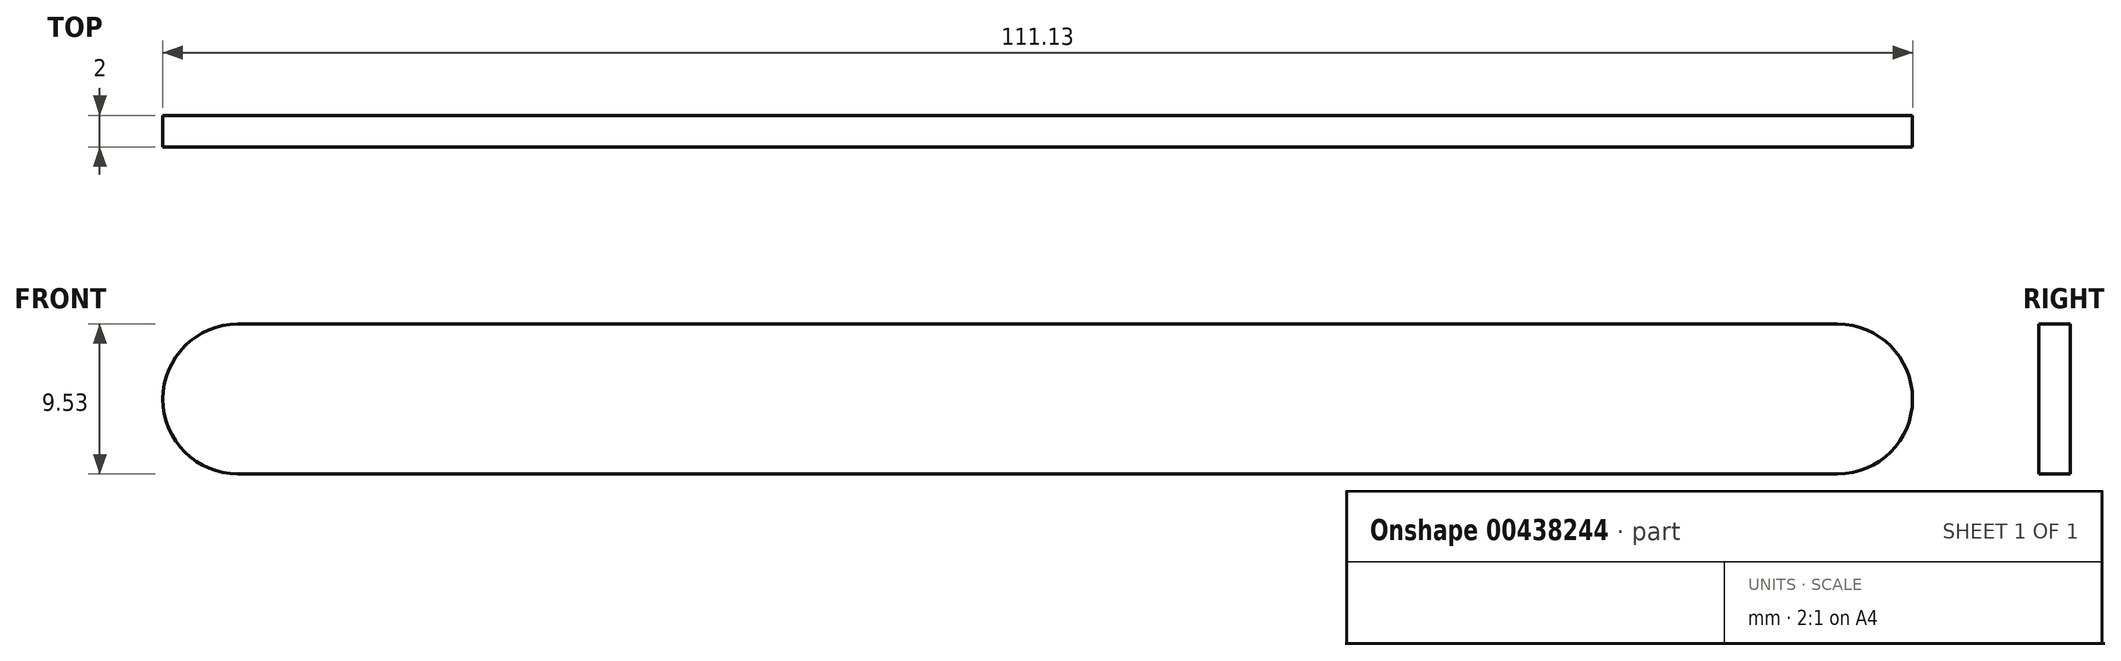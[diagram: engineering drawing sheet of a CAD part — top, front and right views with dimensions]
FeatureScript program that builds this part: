
annotation { "Feature Type Name" : "Feature", "Feature Type Description" : "" }
export const myFeature = defineFeature(function(context is Context, id is Id, definition is map)
    precondition{}
    {
        {
            var Q0;
            Q0=qCreatedBy(makeId("Front.planeOp"),FACE);
            var sketch = newSketch(context, id + "F0", { "sketchPlane" : qUnion([Q0])});
            skLineSegment(sketch, "E0.bottom", {"start": v(-45.28, 32.13) * mm, "end": v(56.32, 32.13) * mm});
            skLineSegment(sketch, "E0.top", {"start": v(-45.28, 22.6) * mm, "end": v(56.32, 22.6) * mm});
            skLineSegment(sketch, "E0.left", {"start": v(-45.28, 32.13) * mm, "end": v(-45.28, 22.6) * mm});
            skLineSegment(sketch, "E0.right", {"start": v(56.32, 32.13) * mm, "end": v(56.32, 22.6) * mm});
            skArc(sketch, "E1", {"start": v(-45.28, 32.13) * mm, "mid": v(-50.04, 27.37) * mm, "end": v(-45.28, 22.6) * mm});
            skArc(sketch, "E2", {"start": v(56.32, 22.6) * mm, "mid": v(61.09, 27.37) * mm, "end": v(56.32, 32.13) * mm});
            skSolve(sketch);
        }
        {
            var Q0;
            Q0=makeQuery(id+"F0.imprint","IMPRINT",FACE,{"disambiguationData":[TD([[makeQuery(id+"F0.imprint","IMPRINT",EDGE,{"derivedFrom":sQuery(id+"F0.wireOp",EDGE,"E0.bottom")}),-1.0]])]});
            var Q1;
            Q1=makeQuery(id+"F0.imprint","IMPRINT",FACE,{"disambiguationData":[TD([[makeQuery(id+"F0.imprint","IMPRINT",EDGE,{"derivedFrom":sQuery(id+"F0.wireOp",EDGE,"E0.left")}),-1.0]])]});
            var Q2;
            Q2=makeQuery(id+"F0.imprint","IMPRINT",FACE,{"disambiguationData":[TD([[makeQuery(id+"F0.imprint","IMPRINT",EDGE,{"derivedFrom":sQuery(id+"F0.wireOp",EDGE,"E0.right")}),1.0]])]});
            extrude(context, id + "F1", {"entities" : qUnion([Q0, Q1, Q2]), "depth" : 2 * mm});
        }
    });
